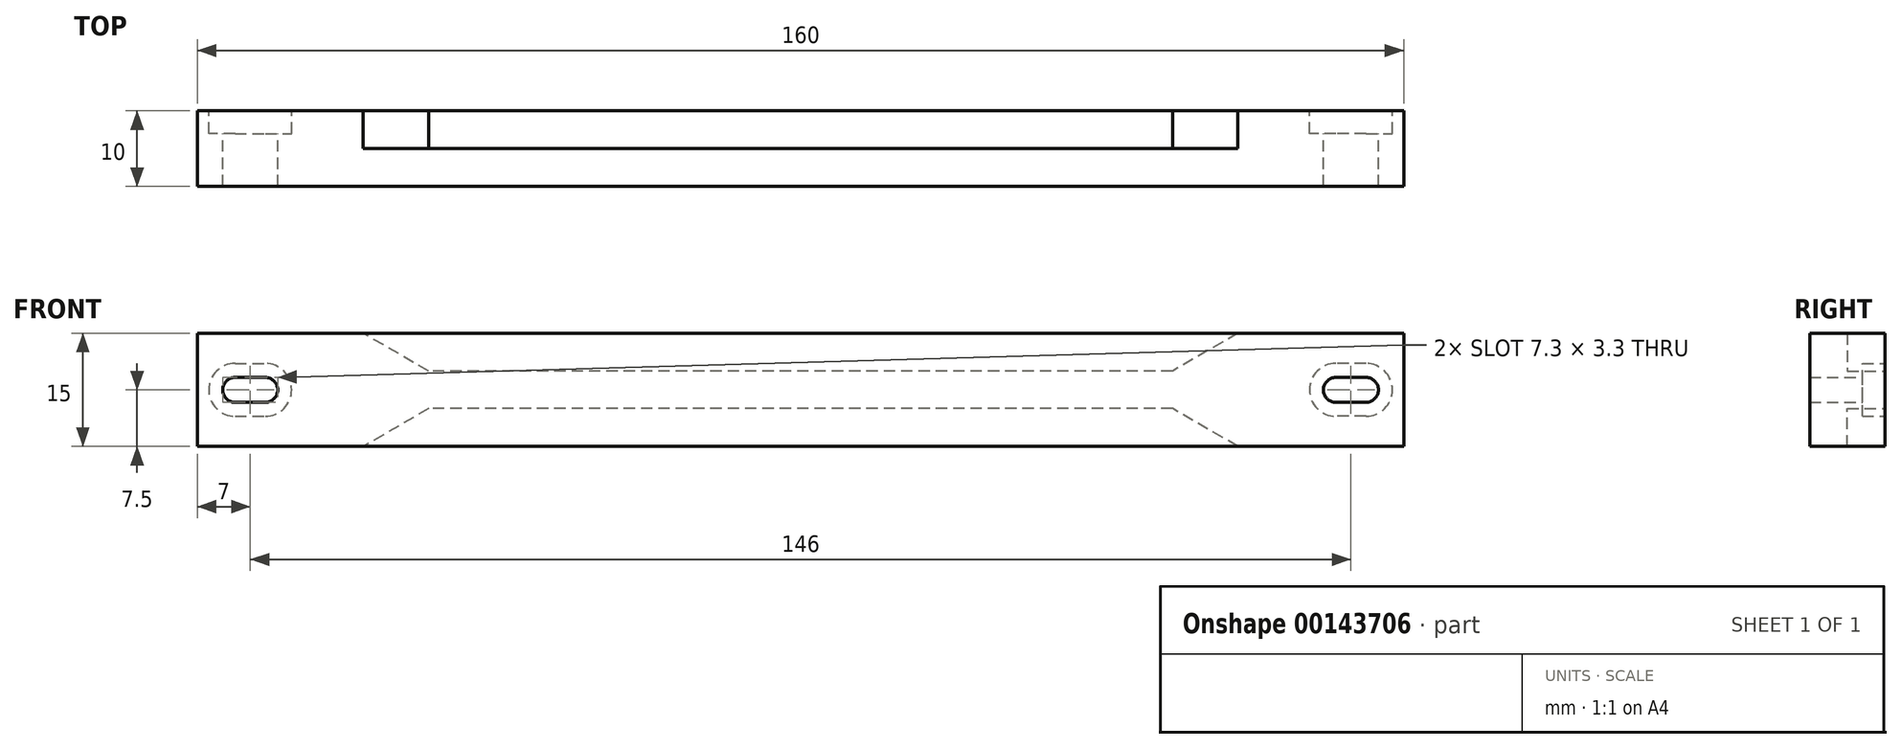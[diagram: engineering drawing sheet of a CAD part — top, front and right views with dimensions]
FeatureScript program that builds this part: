
annotation { "Feature Type Name" : "Feature", "Feature Type Description" : "" }
export const myFeature = defineFeature(function(context is Context, id is Id, definition is map)
    precondition{}
    {
        {
            var Q0;
            Q0=qCreatedBy(makeId("Front.planeOp"),FACE);
            var sketch = newSketch(context, id + "F0", { "sketchPlane" : qUnion([Q0])});
            skLineSegment(sketch, "E0.bottom", {"start": v(80, -7.5) * mm, "end": v(-80, -7.5) * mm});
            skLineSegment(sketch, "E0.top", {"start": v(80, 7.5) * mm, "end": v(-80, 7.5) * mm});
            skLineSegment(sketch, "E0.left", {"start": v(80, -7.5) * mm, "end": v(80, 7.5) * mm});
            skLineSegment(sketch, "E0.right", {"start": v(-80, -7.5) * mm, "end": v(-80, 7.5) * mm});
            skPoint(sketch, "E0.middle", {"position": v(0, 0) * mm});
            skSolve(sketch);
        }
        {
            var Q0;
            Q0 = qSketchRegion(id + "F0", true);
            extrude(context, id + "F1", {"entities" : qUnion([Q0]), "oppositeDirection" : true, "depth" : 10 * mm});
        }
        {
            var Q0;
            Q0=makeQuery(id+"F1.opExtrude","CAP_FACE",FACE,{"disambiguationData":[OSD([sQuery(id+"F0.wireOp",EDGE,"E0.bottom"),sQuery(id+"F0.wireOp",EDGE,"E0.top"),sQuery(id+"F0.wireOp",EDGE,"E0.left"),sQuery(id+"F0.wireOp",EDGE,"E0.right")])],"isStart":false});
            var sketch = newSketch(context, id + "F2", { "sketchPlane" : qUnion([Q0])});
            skLineSegment(sketch, "E1", {"start": v(-58, 7.5) * mm, "end": v(-49.34, 2.5) * mm});
            skLineSegment(sketch, "E2", {"start": v(-49.34, 2.5) * mm, "end": v(49.34, 2.5) * mm});
            skLineSegment(sketch, "E3", {"start": v(49.34, 2.5) * mm, "end": v(58, 7.5) * mm});
            skLineSegment(sketch, "E4", {"start": v(58, 7.5) * mm, "end": v(-58, 7.5) * mm});
            skLineSegment(sketch, "E5", {"start": v(-58, -7.5) * mm, "end": v(-49.34, -2.5) * mm});
            skLineSegment(sketch, "E6", {"start": v(-49.34, -2.5) * mm, "end": v(49.34, -2.5) * mm});
            skLineSegment(sketch, "E7", {"start": v(49.34, -2.5) * mm, "end": v(58, -7.5) * mm});
            skLineSegment(sketch, "E8", {"start": v(58, -7.5) * mm, "end": v(-58, -7.5) * mm});
            skSolve(sketch);
        }
        {
            var Q0;
            Q0 = qSketchRegion(id + "F2", true);
            extrude(context, id + "F3", {"entities" : qUnion([Q0]), "operationType" : NewBodyOperationType.REMOVE, "oppositeDirection" : true, "depth" : 5 * mm});
        }
        {
            var Q0;
            Q0=makeQuery(id+"F1.opExtrude","CAP_FACE",FACE,{"disambiguationData":[OSD([sQuery(id+"F0.wireOp",EDGE,"E0.bottom"),sQuery(id+"F0.wireOp",EDGE,"E0.top"),sQuery(id+"F0.wireOp",EDGE,"E0.left"),sQuery(id+"F0.wireOp",EDGE,"E0.right")])],"isStart":false});
            var sketch = newSketch(context, id + "F4", { "sketchPlane" : qUnion([Q0])});
            skPoint(sketch, "E9", {"position": v(-75, 0) * mm});
            skPoint(sketch, "E10", {"position": v(75, 0) * mm});
            skLineSegment(sketch, "E11", {"start": v(-75, 0) * mm, "end": v(-71, 0) * mm});
            skLineSegment(sketch, "E12", {"start": v(75, 0) * mm, "end": v(71, 0) * mm});
            skArc(sketch, "E13.0.startCap", {"start": v(-75, -1.65) * mm, "mid": v(-76.65, 0) * mm, "end": v(-75, 1.65) * mm});
            skArc(sketch, "E13.0.endCap", {"start": v(-71, 1.65) * mm, "mid": v(-69.35, 0) * mm, "end": v(-71, -1.65) * mm});
            skLineSegment(sketch, "E13.0.left", {"start": v(-75, 1.65) * mm, "end": v(-71, 1.65) * mm});
            skLineSegment(sketch, "E13.0.right", {"start": v(-75, -1.65) * mm, "end": v(-71, -1.65) * mm});
            skArc(sketch, "E14.0.startCap", {"start": v(75, 1.65) * mm, "mid": v(76.65, 0) * mm, "end": v(75, -1.65) * mm});
            skArc(sketch, "E14.0.endCap", {"start": v(71, -1.65) * mm, "mid": v(69.35, 0) * mm, "end": v(71, 1.65) * mm});
            skLineSegment(sketch, "E14.0.left", {"start": v(75, -1.65) * mm, "end": v(71, -1.65) * mm});
            skLineSegment(sketch, "E14.0.right", {"start": v(75, 1.65) * mm, "end": v(71, 1.65) * mm});
            skSolve(sketch);
        }
        {
            var Q0;
            Q0=makeQuery(id+"F1.opExtrude","CAP_FACE",FACE,{"disambiguationData":[OSD([sQuery(id+"F0.wireOp",EDGE,"E0.bottom"),sQuery(id+"F0.wireOp",EDGE,"E0.top"),sQuery(id+"F0.wireOp",EDGE,"E0.left"),sQuery(id+"F0.wireOp",EDGE,"E0.right")])],"isStart":false});
            var sketch = newSketch(context, id + "F5", { "sketchPlane" : qUnion([Q0])});
            skLineSegment(sketch, "E15", {"start": v(-75, 0) * mm, "end": v(-71, 0) * mm});
            skArc(sketch, "E16.0.startCap", {"start": v(-75, -3.5) * mm, "mid": v(-78.5, 0) * mm, "end": v(-75, 3.5) * mm});
            skArc(sketch, "E16.0.endCap", {"start": v(-71, 3.5) * mm, "mid": v(-67.5, 0) * mm, "end": v(-71, -3.5) * mm});
            skLineSegment(sketch, "E16.0.left", {"start": v(-75, 3.5) * mm, "end": v(-71, 3.5) * mm});
            skLineSegment(sketch, "E16.0.right", {"start": v(-75, -3.5) * mm, "end": v(-71, -3.5) * mm});
            skLineSegment(sketch, "E17", {"start": v(75, 0) * mm, "end": v(71, 0) * mm});
            skArc(sketch, "E18.0.startCap", {"start": v(75, 3.5) * mm, "mid": v(78.5, 0) * mm, "end": v(75, -3.5) * mm});
            skArc(sketch, "E18.0.endCap", {"start": v(71, -3.5) * mm, "mid": v(67.5, 0) * mm, "end": v(71, 3.5) * mm});
            skLineSegment(sketch, "E18.0.left", {"start": v(75, -3.5) * mm, "end": v(71, -3.5) * mm});
            skLineSegment(sketch, "E18.0.right", {"start": v(75, 3.5) * mm, "end": v(71, 3.5) * mm});
            skSolve(sketch);
        }
        {
            var Q0;
            Q0 = qSketchRegion(id + "F5", true);
            extrude(context, id + "F6", {"entities" : qUnion([Q0]), "operationType" : NewBodyOperationType.REMOVE, "oppositeDirection" : true, "depth" : 3 * mm});
        }
        {
            var Q0;
            Q0 = qSketchRegion(id + "F4", true);
            extrude(context, id + "F7", {"entities" : qUnion([Q0]), "operationType" : NewBodyOperationType.REMOVE, "endBound" : BoundingType.THROUGH_ALL, "oppositeDirection" : true, "depth" : 25 * mm});
        }
    });
